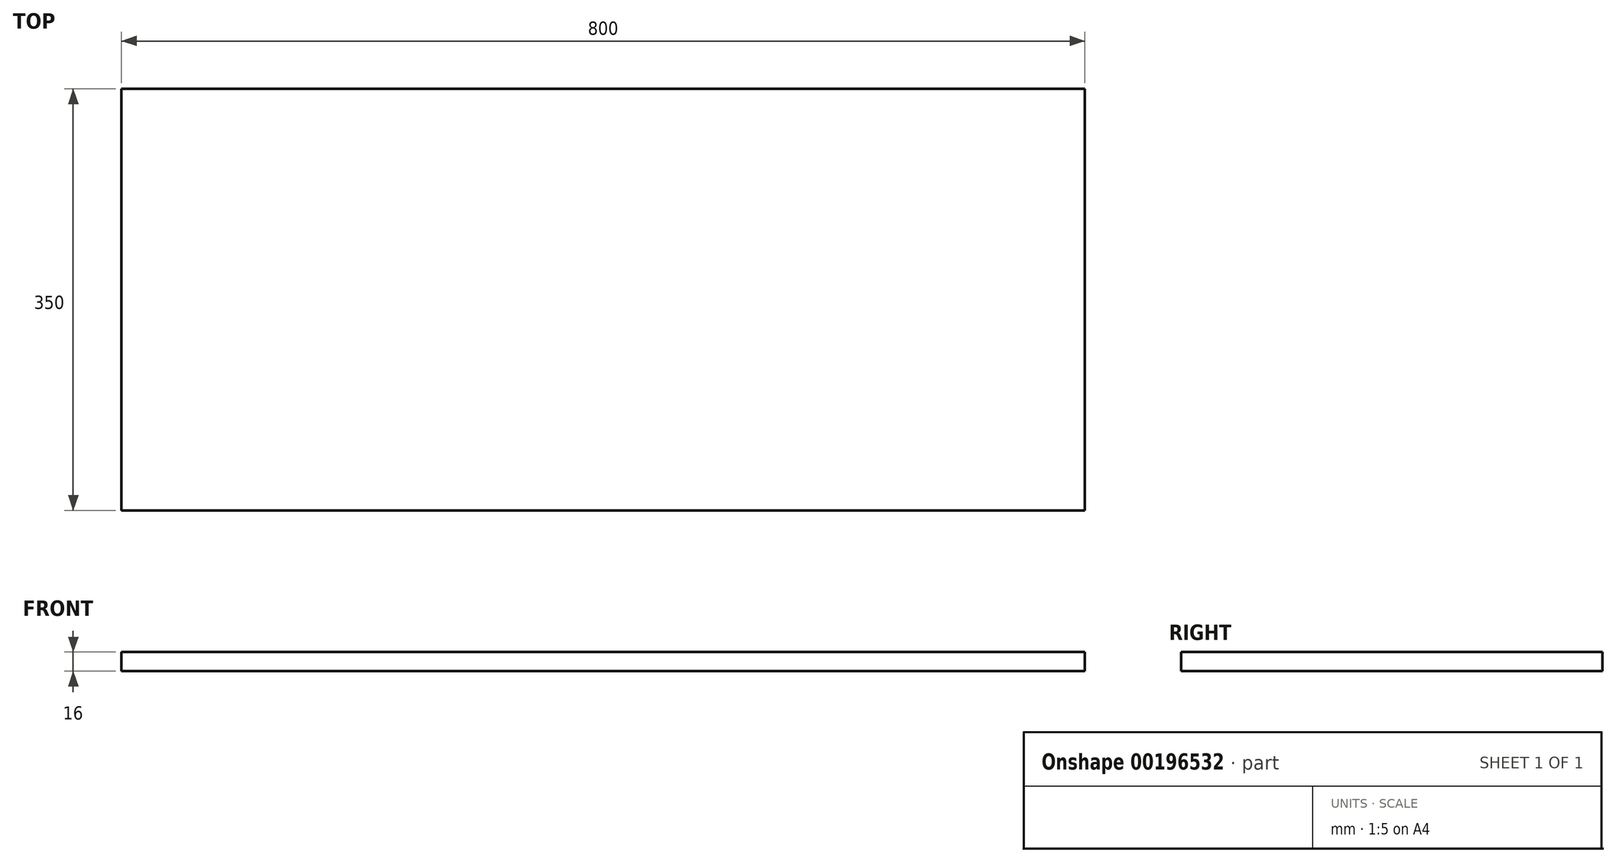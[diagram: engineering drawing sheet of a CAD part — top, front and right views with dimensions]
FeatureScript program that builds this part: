
annotation { "Feature Type Name" : "Feature", "Feature Type Description" : "" }
export const myFeature = defineFeature(function(context is Context, id is Id, definition is map)
    precondition{}
    {
        {
            var Q0;
            Q0=qCreatedBy(makeId("Top.planeOp"),FACE);
            var sketch = newSketch(context, id + "F0", { "sketchPlane" : qUnion([Q0])});
            skLineSegment(sketch, "E0.bottom", {"start": v(-864.34, -235.28) * mm, "end": v(-64.34, -235.28) * mm});
            skLineSegment(sketch, "E0.top", {"start": v(-864.34, 114.72) * mm, "end": v(-64.34, 114.72) * mm});
            skLineSegment(sketch, "E0.left", {"start": v(-864.34, -235.28) * mm, "end": v(-864.34, 114.72) * mm});
            skLineSegment(sketch, "E0.right", {"start": v(-64.34, -235.28) * mm, "end": v(-64.34, 114.72) * mm});
            skSolve(sketch);
        }
        {
            var Q0;
            Q0=makeQuery(id+"F0.imprint","IMPRINT",FACE,{"disambiguationData":[TD([[makeQuery(id+"F0.imprint","IMPRINT",EDGE,{"derivedFrom":sQuery(id+"F0.wireOp",EDGE,"E0.bottom")}),1.0]])]});
            extrude(context, id + "F1", {"entities" : qUnion([Q0]), "depth" : 16 * mm});
        }
    });
